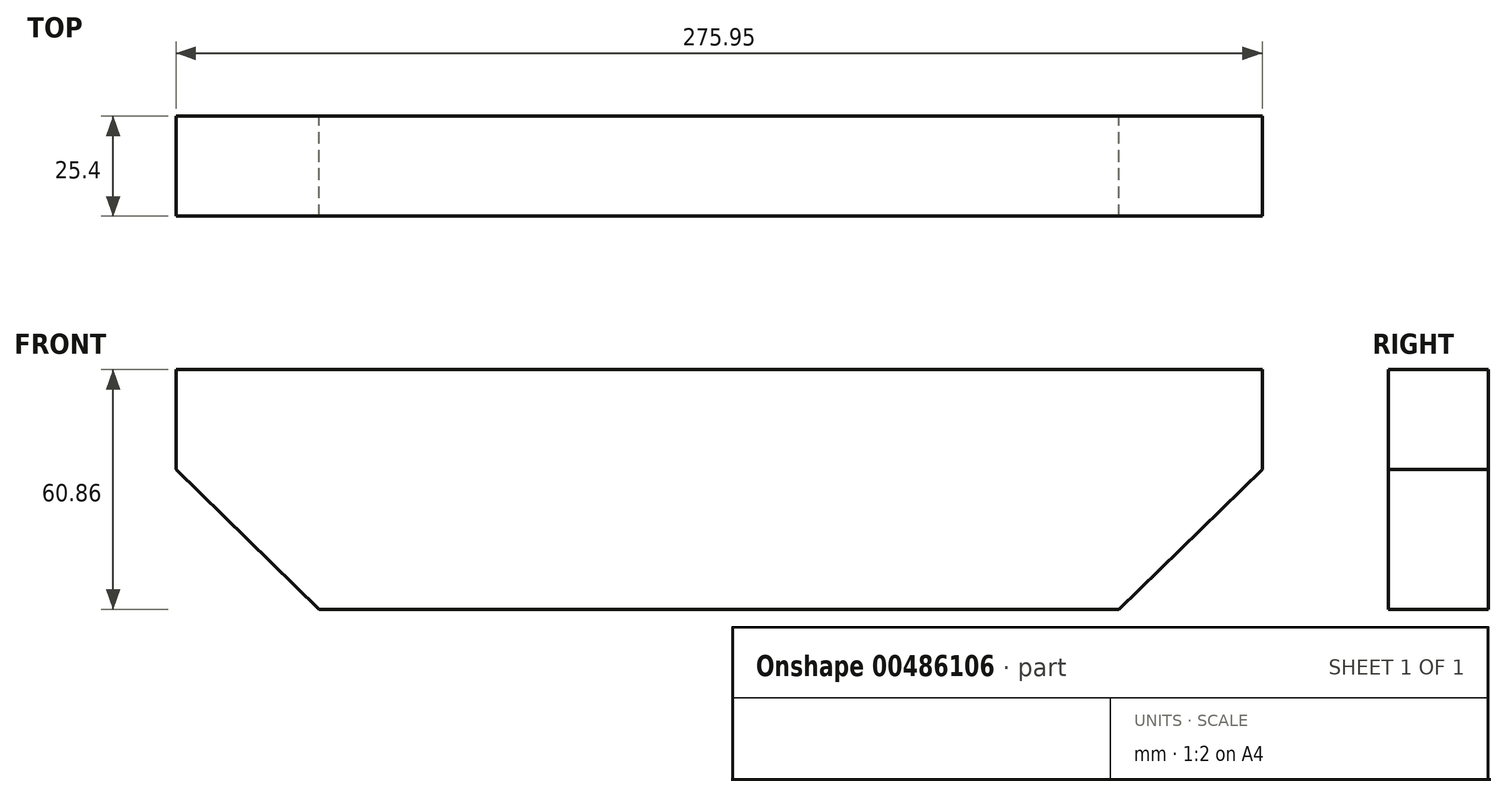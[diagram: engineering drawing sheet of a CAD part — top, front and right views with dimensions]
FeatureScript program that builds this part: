
annotation { "Feature Type Name" : "Feature", "Feature Type Description" : "" }
export const myFeature = defineFeature(function(context is Context, id is Id, definition is map)
    precondition{}
    {
        {
            var Q0;
            Q0=qCreatedBy(makeId("Front.planeOp"),FACE);
            var sketch = newSketch(context, id + "F0", { "sketchPlane" : qUnion([Q0])});
            skLineSegment(sketch, "E0", {"start": v(-162.1, 40.77) * mm, "end": v(113.85, 40.77) * mm});
            skLineSegment(sketch, "E1", {"start": v(113.85, 40.77) * mm, "end": v(113.85, 15.37) * mm});
            skLineSegment(sketch, "E2", {"start": v(113.85, 15.37) * mm, "end": v(77.48, -20.09) * mm});
            skLineSegment(sketch, "E3", {"start": v(77.48, -20.09) * mm, "end": v(-125.72, -20.09) * mm});
            skLineSegment(sketch, "E4", {"start": v(-125.72, -20.09) * mm, "end": v(-162.1, 15.37) * mm});
            skLineSegment(sketch, "E5", {"start": v(-162.1, 15.37) * mm, "end": v(-162.1, 40.77) * mm});
            skSolve(sketch);
        }
        {
            var Q0;
            Q0 = qSketchRegion(id + "F0", true);
            extrude(context, id + "F1", {"entities" : qUnion([Q0]), "depth" : 25.4 * mm});
        }
    });
